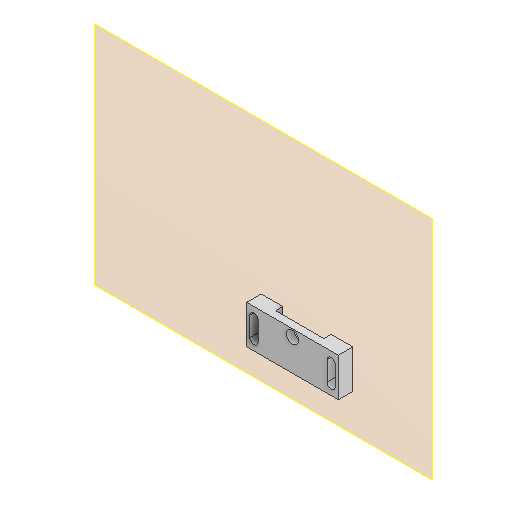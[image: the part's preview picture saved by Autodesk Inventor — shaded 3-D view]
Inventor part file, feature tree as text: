
AUTODESK INVENTOR PART (.ipt)
format: ipt  version: 2022 (Build 260153000, 153)  size: 144,896 bytes
history: native  units: mm
features: other x6, extrude x2, sketch x2, reference x2, projected_geometry x2, plane x1
ambient origin geometry x8: Origin, YZ Plane, XZ Plane, XY Plane, X Axis, Y Axis, Z Axis, Center Point
bodies: Solid1 (feature_tree)
feature tree (15):
  plane  "Work Plane1"
  extrude  "Extrusion1"  Depth=3.4mm
  extrude  "Extrusion2"  TaperAngle=0.0deg  [1 undecoded]
  sketch  "Sketch1"  dims[d0=4.0mm d1=3.4mm]
  reference  "Reference1"
  reference  "Reference2"
  sketch  "Sketch2"  dims[d2=3.4mm d3=0.0mm d4=9.0mm d5=9.0mm d6=0.0mm d7=0.0mm d8=4.0mm d9=4.0mm d10=3.0mm d11=0.0mm d12=5.0mm d13=6.0mm d14=3.0mm d15=3.0mm d16=0.0mm]
  projected_geometry  "Projected Loop1"
  projected_geometry  "Projected Loop2"
  other  "<userpath>\Documents\GitHub\Guinardia\INVENTOR\Assembly_Guinardia_V1.iam"
  other  "Assembly_Guinardia_V1.iam"
  other  "10_Wellplate_base_v1:1"
  other  "<userpath>\Documents\Inventor\Guinardia\INVENTOR\Assembly_Guinardia_V0.iam"
  other  "Assembly_Guinardia_V0.iam"
  other  "10_Wellplate_base:1"
note: 1 required parameter value undecoded (feature->parameter linkage not recoverable at this tier; creation-order binding heuristic only, values carry confidence <= 0.55)
